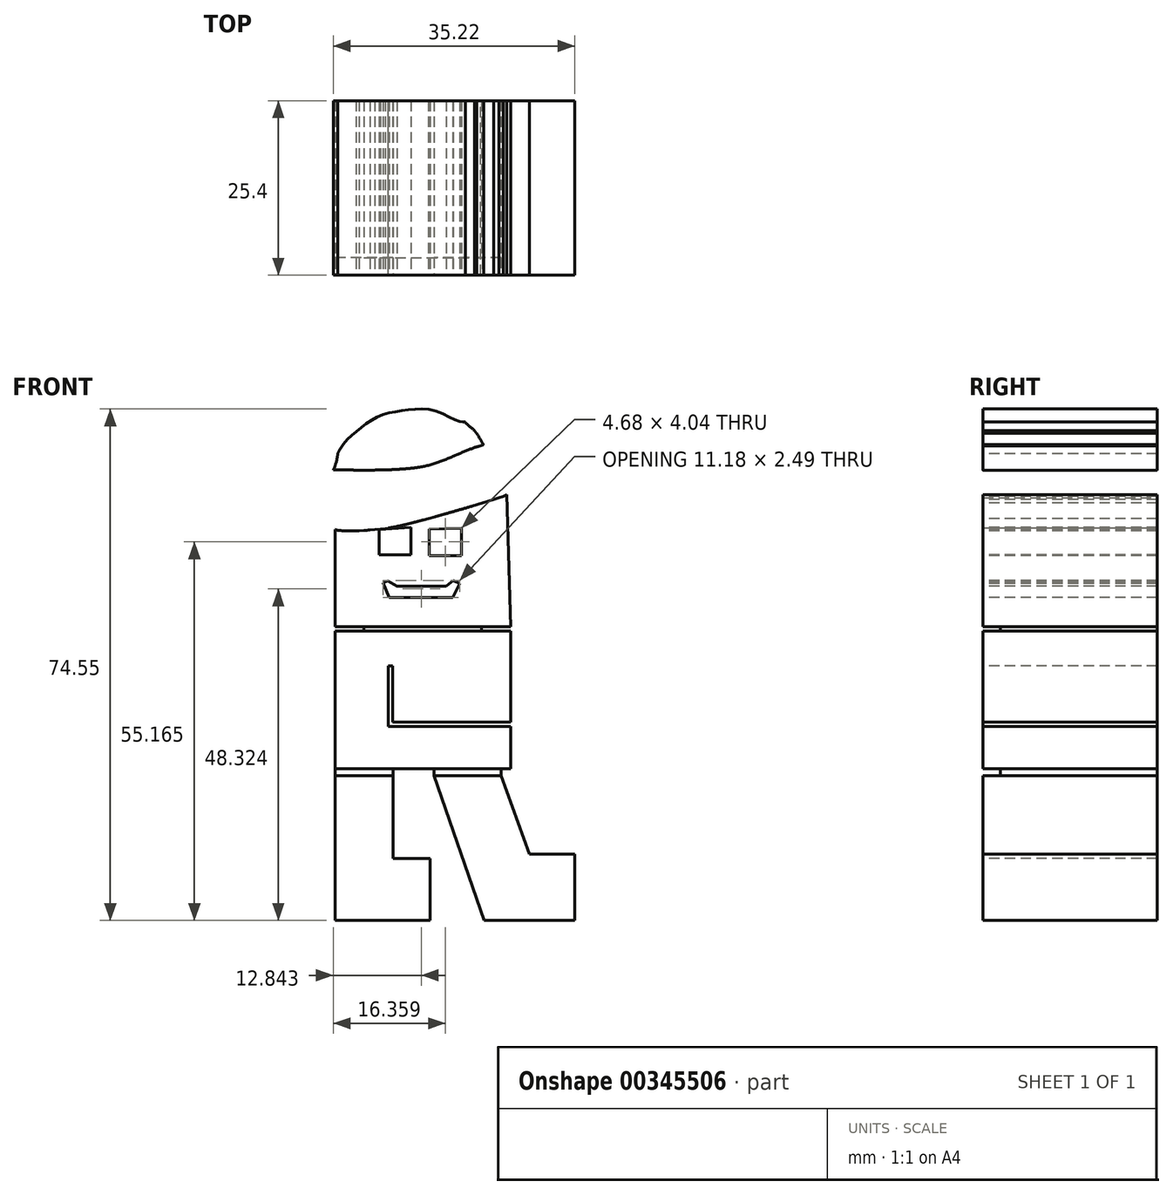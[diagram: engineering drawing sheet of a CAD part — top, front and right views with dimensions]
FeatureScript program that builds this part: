
annotation { "Feature Type Name" : "Feature", "Feature Type Description" : "" }
export const myFeature = defineFeature(function(context is Context, id is Id, definition is map)
    precondition{}
    {
        {
            var Q0;
            Q0=qCreatedBy(makeId("Front.planeOp"),FACE);
            var sketch = newSketch(context, id + "F0", { "sketchPlane" : qUnion([Q0])});
            skLineSegment(sketch, "E0", {"start": v(-88.68, 24.26) * mm, "end": v(-88.68, 10.11) * mm});
            skLineSegment(sketch, "E1", {"start": v(-88.68, -11) * mm, "end": v(-88.68, -32.7) * mm});
            skLineSegment(sketch, "E2", {"start": v(-88.68, -32.7) * mm, "end": v(-74.81, -32.7) * mm});
            skLineSegment(sketch, "E3", {"start": v(-74.81, -32.7) * mm, "end": v(-74.81, -23.66) * mm});
            skLineSegment(sketch, "E4", {"start": v(-74.81, -23.66) * mm, "end": v(-80.24, -23.66) * mm});
            skLineSegment(sketch, "E5", {"start": v(-80.24, -23.66) * mm, "end": v(-80.24, -11.6) * mm});
            skLineSegment(sketch, "E6", {"start": v(-74.25, -11.6) * mm, "end": v(-64.48, -11.6) * mm});
            skLineSegment(sketch, "E7", {"start": v(-63.06, -10.58) * mm, "end": v(-63.06, 9.5) * mm});
            skLineSegment(sketch, "E8", {"start": v(-63.06, 9.5) * mm, "end": v(-88.68, 9.5) * mm});
            skLineSegment(sketch, "E9", {"start": v(-88.68, 0) * mm, "end": v(-88.68, -11) * mm});
            skLineSegment(sketch, "E10", {"start": v(-88.68, 9.5) * mm, "end": v(-88.68, 0) * mm});
            skLineSegment(sketch, "E11", {"start": v(-63.66, 29.38) * mm, "end": v(-63.08, 10.11) * mm});
            skLineSegment(sketch, "E12", {"start": v(-53.72, -31.8) * mm, "end": v(-53.72, -23.05) * mm});
            skLineSegment(sketch, "E13", {"start": v(-53.72, -23.05) * mm, "end": v(-60.35, -23.05) * mm});
            skLineSegment(sketch, "E14", {"start": v(-60.35, -23.05) * mm, "end": v(-64.48, -11.6) * mm});
            skLineSegment(sketch, "E15", {"start": v(-64.48, -11.6) * mm, "end": v(-71.65, -11.6) * mm});
            skLineSegment(sketch, "E16", {"start": v(-80.88, 4.41) * mm, "end": v(-80.88, -4.44) * mm});
            skLineSegment(sketch, "E17", {"start": v(-80.88, -4.44) * mm, "end": v(-63.06, -4.44) * mm});
            skLineSegment(sketch, "E18", {"start": v(-63.06, -4.44) * mm, "end": v(-80.88, -4.44) * mm});
            skLineSegment(sketch, "E19", {"start": v(-82.23, 24.26) * mm, "end": v(-82.23, 20.6) * mm});
            skLineSegment(sketch, "E20", {"start": v(-82.23, 20.6) * mm, "end": v(-77.62, 20.6) * mm});
            skLineSegment(sketch, "E21", {"start": v(-77.62, 20.6) * mm, "end": v(-77.62, 24.6) * mm});
            skLineSegment(sketch, "E22", {"start": v(-77.62, 24.6) * mm, "end": v(-82.23, 24.26) * mm});
            skLineSegment(sketch, "E23", {"start": v(-74.92, 24.36) * mm, "end": v(-74.92, 20.44) * mm});
            skLineSegment(sketch, "E24", {"start": v(-74.92, 20.44) * mm, "end": v(-70.24, 20.45) * mm});
            skLineSegment(sketch, "E25", {"start": v(-70.24, 20.45) * mm, "end": v(-70.24, 24.49) * mm});
            skLineSegment(sketch, "E26", {"start": v(-70.24, 24.49) * mm, "end": v(-74.92, 24.36) * mm});
            skLineSegment(sketch, "E27", {"start": v(-81.69, 16.53) * mm, "end": v(-80.8, 14.38) * mm});
            skLineSegment(sketch, "E28", {"start": v(-80.8, 14.38) * mm, "end": v(-71.52, 14.38) * mm});
            skLineSegment(sketch, "E29", {"start": v(-71.52, 14.38) * mm, "end": v(-70.5, 16.41) * mm});
            skLineSegment(sketch, "E30", {"start": v(-70.5, 16.41) * mm, "end": v(-71.42, 16.87) * mm});
            skLineSegment(sketch, "E31", {"start": v(-71.42, 16.87) * mm, "end": v(-72.48, 16) * mm});
            skLineSegment(sketch, "E32", {"start": v(-72.48, 16) * mm, "end": v(-79.65, 16) * mm});
            skLineSegment(sketch, "E33", {"start": v(-79.65, 16) * mm, "end": v(-80.97, 16.77) * mm});
            skLineSegment(sketch, "E34", {"start": v(-80.97, 16.77) * mm, "end": v(-81.69, 16.53) * mm});
            skLineSegment(sketch, "E35", {"start": v(-94.06, 32.86) * mm, "end": v(-88.68, 24.26) * mm});
            skPoint(sketch, "E36.6.internal.snap0", {"position": v(-63.29, 34.39) * mm});
            skFitSpline(sketch, "E37", {"points": [v(-69.7, 39.96) * mm, v(-66.1, 40.04) * mm, v(-62.91, 39.4) * mm, v(-64.66, 37.64) * mm, v(-66.76, 36.73) * mm, v(-67, 36.64) * mm, v(-68.34, 38.66) * mm, v(-69.7, 39.96) * mm]});
            skFitSpline(sketch, "E38", {"points": [v(-88.94, 32.95) * mm, v(-87.97, 35.93) * mm, v(-85.54, 38.6) * mm, v(-82.35, 40.76) * mm, v(-78.48, 41.64) * mm, v(-74, 41.56) * mm, v(-70.41, 39.96) * mm, v(-69.7, 39.96) * mm, v(-68.34, 38.66) * mm, v(-67, 36.64) * mm, v(-67.47, 36.47) * mm, v(-71.33, 35) * mm, v(-75.64, 33.5) * mm, v(-80.95, 32.98) * mm, v(-85.62, 32.92) * mm, v(-88.45, 32.94) * mm, v(-88.94, 32.95) * mm]});
            skLineSegment(sketch, "E39", {"start": v(-74.25, -11.6) * mm, "end": v(-67.28, -31.8) * mm});
            skLineSegment(sketch, "E40", {"start": v(-80.24, -11.6) * mm, "end": v(-88.68, -11.6) * mm});
            skLineSegment(sketch, "E41", {"start": v(-80.88, 4.41) * mm, "end": v(-80.3, 4.41) * mm});
            skLineSegment(sketch, "E42", {"start": v(-80.3, 4.41) * mm, "end": v(-80.3, -3.8) * mm});
            skLineSegment(sketch, "E43", {"start": v(-80.3, -3.8) * mm, "end": v(-63.06, -3.8) * mm});
            skLineSegment(sketch, "E44", {"start": v(-63.06, -3.8) * mm, "end": v(-63.06, -4.44) * mm});
            skLineSegment(sketch, "E45", {"start": v(-63.06, -10.58) * mm, "end": v(-88.68, -10.58) * mm});
            skLineSegment(sketch, "E46", {"start": v(-88.68, 10.11) * mm, "end": v(-63.08, 10.11) * mm});
            skLineSegment(sketch, "E47", {"start": v(-88.86, 24.55) * mm, "end": v(-87.68, 24.41) * mm});
            skLineSegment(sketch, "E48", {"start": v(-87.68, 24.41) * mm, "end": v(-86.54, 24.42) * mm});
            skLineSegment(sketch, "E49", {"start": v(-86.54, 24.42) * mm, "end": v(-85.24, 24.47) * mm});
            skLineSegment(sketch, "E50", {"start": v(-85.24, 24.47) * mm, "end": v(-83.56, 24.53) * mm});
            skLineSegment(sketch, "E51", {"start": v(-83.56, 24.53) * mm, "end": v(-82.4, 24.62) * mm});
            skLineSegment(sketch, "E52", {"start": v(-82.4, 24.62) * mm, "end": v(-81.11, 24.83) * mm});
            skLineSegment(sketch, "E53", {"start": v(-81.11, 24.83) * mm, "end": v(-80.18, 24.98) * mm});
            skLineSegment(sketch, "E54", {"start": v(-80.18, 24.98) * mm, "end": v(-78.82, 25.25) * mm});
            skLineSegment(sketch, "E55", {"start": v(-78.82, 25.25) * mm, "end": v(-77.24, 25.65) * mm});
            skLineSegment(sketch, "E56", {"start": v(-77.24, 25.65) * mm, "end": v(-75.2, 26.19) * mm});
            skLineSegment(sketch, "E57", {"start": v(-75.2, 26.19) * mm, "end": v(-73.38, 26.67) * mm});
            skLineSegment(sketch, "E58", {"start": v(-73.38, 26.67) * mm, "end": v(-70.5, 27.43) * mm});
            skLineSegment(sketch, "E59", {"start": v(-70.5, 27.43) * mm, "end": v(-68.35, 28.1) * mm});
            skLineSegment(sketch, "E60", {"start": v(-68.35, 28.1) * mm, "end": v(-65.9, 28.87) * mm});
            skLineSegment(sketch, "E61", {"start": v(-65.9, 28.87) * mm, "end": v(-63.58, 29.7) * mm});
            skLineSegment(sketch, "E62", {"start": v(-63.58, 29.7) * mm, "end": v(-63.56, 29.51) * mm});
            skLineSegment(sketch, "E63", {"start": v(-63.56, 29.51) * mm, "end": v(-63.58, 29.46) * mm});
            skLineSegment(sketch, "E64", {"start": v(-63.58, 29.46) * mm, "end": v(-63.64, 29.38) * mm});
            skLineSegment(sketch, "E65", {"start": v(-63.64, 29.38) * mm, "end": v(-64.17, 29.1) * mm});
            skLineSegment(sketch, "E66", {"start": v(-64.17, 29.1) * mm, "end": v(-64.76, 28.92) * mm});
            skLineSegment(sketch, "E67", {"start": v(-64.76, 28.92) * mm, "end": v(-65.57, 28.63) * mm});
            skLineSegment(sketch, "E68", {"start": v(-65.57, 28.63) * mm, "end": v(-67.18, 28.12) * mm});
            skLineSegment(sketch, "E69", {"start": v(-67.18, 28.12) * mm, "end": v(-68.65, 27.7) * mm});
            skLineSegment(sketch, "E70", {"start": v(-68.65, 27.7) * mm, "end": v(-70.9, 27.04) * mm});
            skLineSegment(sketch, "E71", {"start": v(-70.9, 27.04) * mm, "end": v(-72.9, 26.47) * mm});
            skLineSegment(sketch, "E72", {"start": v(-72.9, 26.47) * mm, "end": v(-74.1, 26.14) * mm});
            skLineSegment(sketch, "E73", {"start": v(-74.1, 26.14) * mm, "end": v(-75.04, 25.88) * mm});
            skLineSegment(sketch, "E74", {"start": v(-75.04, 25.88) * mm, "end": v(-75.78, 25.68) * mm});
            skLineSegment(sketch, "E75", {"start": v(-75.78, 25.68) * mm, "end": v(-76.6, 25.46) * mm});
            skLineSegment(sketch, "E76", {"start": v(-76.6, 25.46) * mm, "end": v(-77.32, 25.27) * mm});
            skLineSegment(sketch, "E77", {"start": v(-77.32, 25.27) * mm, "end": v(-78.28, 25.03) * mm});
            skLineSegment(sketch, "E78", {"start": v(-78.28, 25.03) * mm, "end": v(-79.17, 24.83) * mm});
            skLineSegment(sketch, "E79", {"start": v(-79.17, 24.83) * mm, "end": v(-79.7, 24.7) * mm});
            skLineSegment(sketch, "E80", {"start": v(-79.7, 24.7) * mm, "end": v(-80.33, 24.6) * mm});
            skLineSegment(sketch, "E81", {"start": v(-80.33, 24.6) * mm, "end": v(-80.9, 24.5) * mm});
            skLineSegment(sketch, "E82", {"start": v(-80.9, 24.5) * mm, "end": v(-81.34, 24.42) * mm});
            skLineSegment(sketch, "E83", {"start": v(-81.34, 24.42) * mm, "end": v(-82.06, 24.33) * mm});
            skLineSegment(sketch, "E84", {"start": v(-82.06, 24.33) * mm, "end": v(-82.88, 24.25) * mm});
            skLineSegment(sketch, "E85", {"start": v(-82.88, 24.25) * mm, "end": v(-83.6, 24.2) * mm});
            skLineSegment(sketch, "E86", {"start": v(-83.6, 24.2) * mm, "end": v(-85.15, 24.1) * mm});
            skLineSegment(sketch, "E87", {"start": v(-85.15, 24.1) * mm, "end": v(-86.6, 24.08) * mm});
            skLineSegment(sketch, "E88", {"start": v(-86.6, 24.08) * mm, "end": v(-87.42, 24.1) * mm});
            skLineSegment(sketch, "E89", {"start": v(-87.42, 24.1) * mm, "end": v(-88.06, 24.14) * mm});
            skLineSegment(sketch, "E90", {"start": v(-88.06, 24.14) * mm, "end": v(-88.56, 24.22) * mm});
            skLineSegment(sketch, "E91", {"start": v(-88.56, 24.22) * mm, "end": v(-88.67, 24.26) * mm});
            skLineSegment(sketch, "E92", {"start": v(-88.67, 24.26) * mm, "end": v(-88.86, 24.55) * mm});
            skLineSegment(sketch, "E93", {"start": v(-88.37, 35.84) * mm, "end": v(-87.97, 35.93) * mm});
            skFitSpline(sketch, "E94.trimOffspring", {"points": [v(-88.68, 24.26) * mm, v(-82.83, 24.26) * mm, v(-75.78, 25.68) * mm, v(-63.66, 29.38) * mm, v(-63.62, 29.96) * mm, v(-62.91, 39.4) * mm, v(-63.29, 38.66) * mm, v(-70.15, 35.5) * mm, v(-77.62, 33.2) * mm, v(-94.06, 32.86) * mm, v(-93.78, 32.4) * mm, v(-89.18, 25.06) * mm, v(-88.68, 24.26) * mm]});
            skFitSpline(sketch, "E95.trimOffspring", {"points": [v(-94.06, 32.86) * mm, v(-91.65, 34.7) * mm, v(-88.37, 35.84) * mm, v(-88.94, 32.95) * mm, v(-89.32, 32.95) * mm, v(-94.06, 32.86) * mm]});
            skLineSegment(sketch, "E96.trimOffspring", {"start": v(-63.62, 29.96) * mm, "end": v(-63.66, 29.38) * mm});
            skLineSegment(sketch, "E97", {"start": v(-84.5, 10.11) * mm, "end": v(-84.5, 9.5) * mm});
            skLineSegment(sketch, "E98", {"start": v(-67.34, 10.11) * mm, "end": v(-67.34, 9.5) * mm});
            skLineSegment(sketch, "E99", {"start": v(-80.24, -11.6) * mm, "end": v(-80.24, -10.58) * mm});
            skLineSegment(sketch, "E100", {"start": v(-74.25, -11.6) * mm, "end": v(-74.25, -10.58) * mm});
            skPoint(sketch, "E100.endSnap0", {"position": v(-75.87, -10.58) * mm});
            skLineSegment(sketch, "E101", {"start": v(-64.48, -11.6) * mm, "end": v(-64.48, -10.58) * mm});
            skPoint(sketch, "E102.orphan", {"position": v(-63.06, -11.6) * mm});
            skLineSegment(sketch, "E103", {"start": v(-53.72, -32.7) * mm, "end": v(-67.28, -32.7) * mm});
            skLineSegment(sketch, "E104", {"start": v(-67.28, -31.8) * mm, "end": v(-66.97, -32.7) * mm});
            skLineSegment(sketch, "E105", {"start": v(-53.72, -31.8) * mm, "end": v(-53.72, -32.7) * mm});
            skSolve(sketch);
        }
        {
            var Q0;
            {var subQ9=sQuery(id+"F0.wireOp",EDGE,"E38");Q0=makeQuery(id+"F0.imprint","IMPRINT",FACE,{"disambiguationData":[TD([[makeQuery(id+"F0.imprint","IMPRINT",EDGE,{"derivedFrom":subQ9}),-1.0]])]});}
            extrude(context, id + "F1", {"entities" : qUnion([Q0]), "oppositeDirection" : true, "depth" : 25.4 * mm});
        }
        {
            var Q0;
            {var subQ0=sQuery(id+"F0.wireOp",EDGE,"E10");Q0=makeQuery(id+"F0.imprint","IMPRINT",FACE,{"disambiguationData":[TD([[makeQuery(id+"F0.imprint","IMPRINT",EDGE,{"derivedFrom":subQ0}),1.0]])]});}
            var Q1;
            {var subQ4=sQuery(id+"F0.wireOp",EDGE,"E40");Q1=makeQuery(id+"F0.imprint","IMPRINT",FACE,{"disambiguationData":[TD([[makeQuery(id+"F0.imprint","IMPRINT",EDGE,{"derivedFrom":subQ4}),-1.0]])]});}
            var Q2;
            {var subQ1=sQuery(id+"F0.wireOp",EDGE,"E2");Q2=makeQuery(id+"F0.imprint","IMPRINT",FACE,{"disambiguationData":[TD([[makeQuery(id+"F0.imprint","IMPRINT",EDGE,{"derivedFrom":subQ1}),1.0]])]});}
            var Q3;
            Q3=makeQuery(id+"F0.imprint","IMPRINT",FACE,{"disambiguationData":[TD([[makeQuery(id+"F0.imprint","IMPRINT",EDGE,{"derivedFrom":sQuery(id+"F0.wireOp",EDGE,"E6")}),-1.0]])]});
            var Q4;
            Q4=makeQuery(id+"F0.imprint","IMPRINT",FACE,{"disambiguationData":[TD([[makeQuery(id+"F0.imprint","IMPRINT",EDGE,{"derivedFrom":sQuery(id+"F0.wireOp",EDGE,"E6")}),1.0]])]});
            var Q5;
            {var subQ30=sQuery(id+"F0.wireOp",EDGE,"E0");Q5=makeQuery(id+"F0.imprint","IMPRINT",FACE,{"disambiguationData":[TD([[makeQuery(id+"F0.imprint","IMPRINT",EDGE,{"derivedFrom":subQ30}),1.0]])]});}
            var Q6;
            {var subQ0=sQuery(id+"F0.wireOp",EDGE,"E97");Q6=makeQuery(id+"F0.imprint","IMPRINT",FACE,{"disambiguationData":[TD([[makeQuery(id+"F0.imprint","IMPRINT",EDGE,{"derivedFrom":subQ0}),1.0]])]});}
            extrude(context, id + "F2", {"entities" : qUnion([Q0, Q1, Q2, Q3, Q4, Q5, Q6]), "oppositeDirection" : true, "depth" : 25.4 * mm});
        }
        {
            var Q0;
            {var subQ0=sQuery(id+"F0.wireOp",EDGE,"E40");Q0=makeQuery(id+"F0.imprint","IMPRINT",FACE,{"disambiguationData":[TD([[makeQuery(id+"F0.imprint","IMPRINT",EDGE,{"derivedFrom":subQ0}),-1.0]])]});}
            var Q1;
            Q1=makeQuery(id+"F0.imprint","IMPRINT",FACE,{"disambiguationData":[TD([[makeQuery(id+"F0.imprint","IMPRINT",EDGE,{"derivedFrom":sQuery(id+"F0.wireOp",EDGE,"E6")}),1.0]])]});
            extrude(context, id + "F3", {"entities" : qUnion([Q0, Q1]), "operationType" : NewBodyOperationType.REMOVE, "oppositeDirection" : true, "depth" : 2.54 * mm});
        }
        {
            var Q0;
            {var subQ0=sQuery(id+"F0.wireOp",EDGE,"E97");Q0=makeQuery(id+"F0.imprint","IMPRINT",FACE,{"disambiguationData":[TD([[makeQuery(id+"F0.imprint","IMPRINT",EDGE,{"derivedFrom":subQ0}),1.0]])]});}
            extrude(context, id + "F4", {"entities" : qUnion([Q0]), "operationType" : NewBodyOperationType.REMOVE, "oppositeDirection" : true, "depth" : 2.54 * mm});
        }
    });
